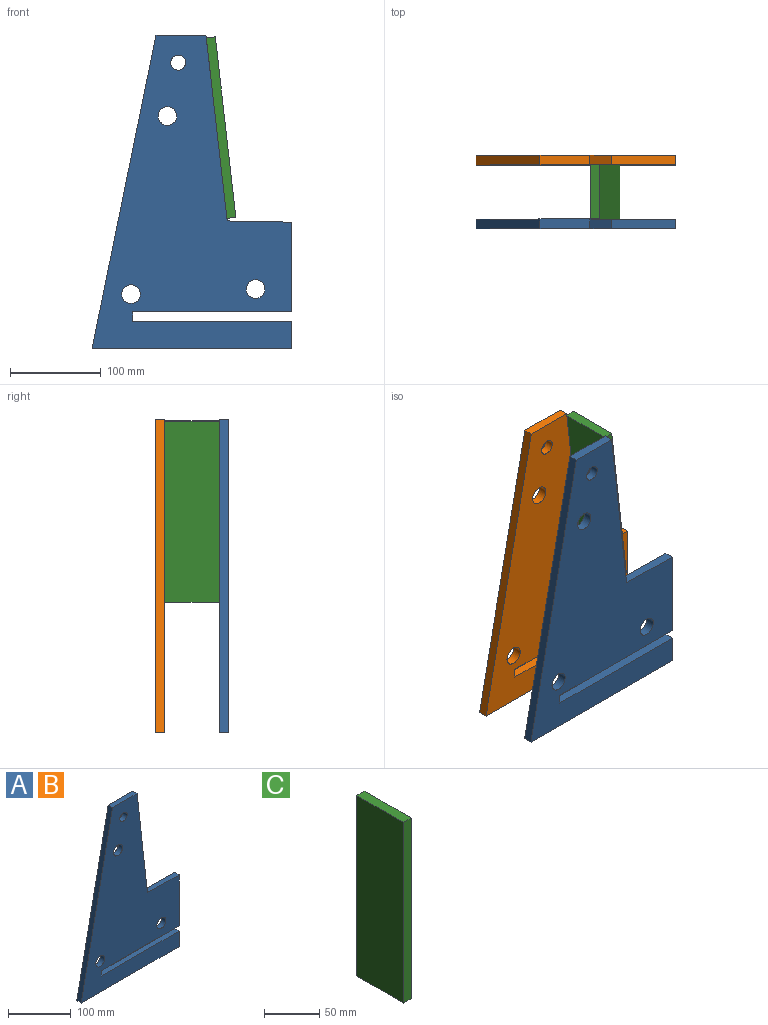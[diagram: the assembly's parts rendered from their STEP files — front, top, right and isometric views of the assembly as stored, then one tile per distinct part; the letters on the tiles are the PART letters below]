
ASSEMBLY  parts=3 mates=2
PART A: 16 faces, bbox 220x10x344.7 mm
  f0: plane 175x10mm, normal (0,0,-1), area 1750mm2, adj f1,f12,f14,f15
  f1: plane 98.68x10mm, normal (1,0,0), area 986.8mm2, adj f0,f2,f14,f15
  f2: plane 71.33x10mm, normal (0.02,0,1), area 713.4mm2, adj f1,f3,f14,f15
  f3: plane 204.23x23.3mm, normal (0.99,0,0.11), area 2055.6mm2, adj f2,f4,f14,f15
  f4: plane 55x10mm, normal (0,0,1), area 550mm2, adj f3,f5,f14,f15
  f5: plane 344.75x70.37mm, normal (-0.98,0,0.2), area 3518.6mm2, adj f4,f6,f14,f15
  f6: plane 220x10mm, normal (0,0,-1), area 2200mm2, adj f5,f7,f14,f15
  f7: plane 30x10mm, normal (1,0,0), area 300mm2, adj f6,f8,f14,f15
  f8: plane 175x10mm, normal (0,0,1), area 1750mm2, adj f7,f12,f14,f15
  f9: cylinder r=10.25mm len=20.5mm, axis (0,1,0), area 644mm2, adj f14,f15
  f10: cylinder r=10.25mm len=20.5mm, axis (0,1,0), area 644mm2, adj f14,f15
  f11: cylinder r=10.25mm len=20.5mm, axis (0,1,0), area 644mm2, adj f14,f15
  f12: plane 10.5x10mm, normal (1,0,0), area 105mm2, adj f0,f8,f14,f15
  f13: cylinder r=8.25mm len=16.5mm, axis (0,1,0), area 518.4mm2, adj f14,f15
  f14: plane 344.75x220mm, normal (0,-1,0), area 43678.2mm2, adj f0,f1,f2,f3,f4,f5,f6,f7
  f15: plane 344.75x220mm, normal (0,1,0), area 43678.2mm2, adj f0,f1,f2,f3,f4,f5,f6,f7
PART B: same geometry as A
PART C: 6 faces, bbox 10x60x200 mm
  f0: plane 60x10mm, normal (0,0,1), area 600mm2, adj f1,f3,f4,f5
  f1: plane 200x60mm, normal (1,0,0), area 12000mm2, adj f0,f2,f4,f5
  f2: plane 60x10mm, normal (0,0,-1), area 600mm2, adj f1,f3,f4,f5
  f3: plane 200x60mm, normal (-1,0,0), area 12000mm2, adj f0,f2,f4,f5
  f4: plane 200x10mm, normal (0,1,0), area 2000mm2, adj f0,f1,f2,f3
  f5: plane 200x10mm, normal (0,-1,0), area 2000mm2, adj f0,f1,f2,f3
PLACE A t=(-32.21,-427.1,-5.01)mm
PLACE B t=(-32.21,-357.1,-5.01)mm fixed
PLACE C rot(axis=(0,1,0),173.5deg) t=(-246.81,-427.1,1949.5)mm
MATE fastened A.f3 <-> C.f1  axis (0.99,0,0.11) through (-78.05,-427.1,977.62)mm
MATE fastened B.f10 <-> A.f10  axis (0,-1,0) through (-172.21,-367.1,794.99)mm
